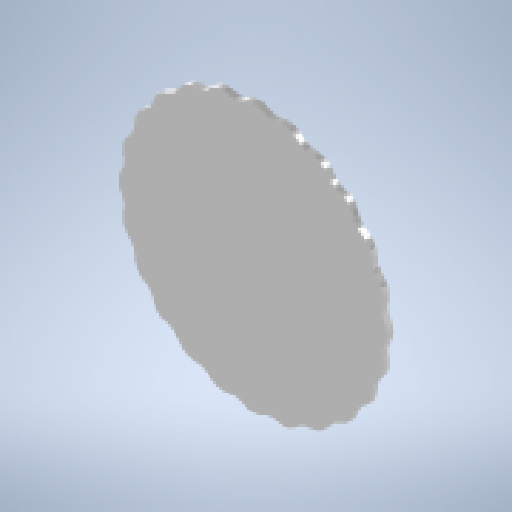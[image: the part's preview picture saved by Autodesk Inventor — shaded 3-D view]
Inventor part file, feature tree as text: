
AUTODESK INVENTOR PART (.ipt)
format: ipt  version: 2024 (Build 280153000, 153)  size: 312,320 bytes
history: native  units: mm
features: other x2, sketch x2, extrude x1, hole x1
ambient origin geometry x8: Origin, YZ Plane, XZ Plane, XY Plane, X Axis, Y Axis, Z Axis, Center Point
bodies: Body1 (feature_tree)
feature tree (6):
  other  "ソリッド1"
  extrude  "押し出し1"  Depth=3600.0mm TaperAngle=0.0deg
  hole  "穴1"  [1 undecoded]
  sketch  "スケッチ1"
  other  "2D 計算式曲線1"
  sketch  "スケッチ2"
note: 1 required parameter value undecoded (feature->parameter linkage not recoverable at this tier; creation-order binding heuristic only, values carry confidence <= 0.55)
